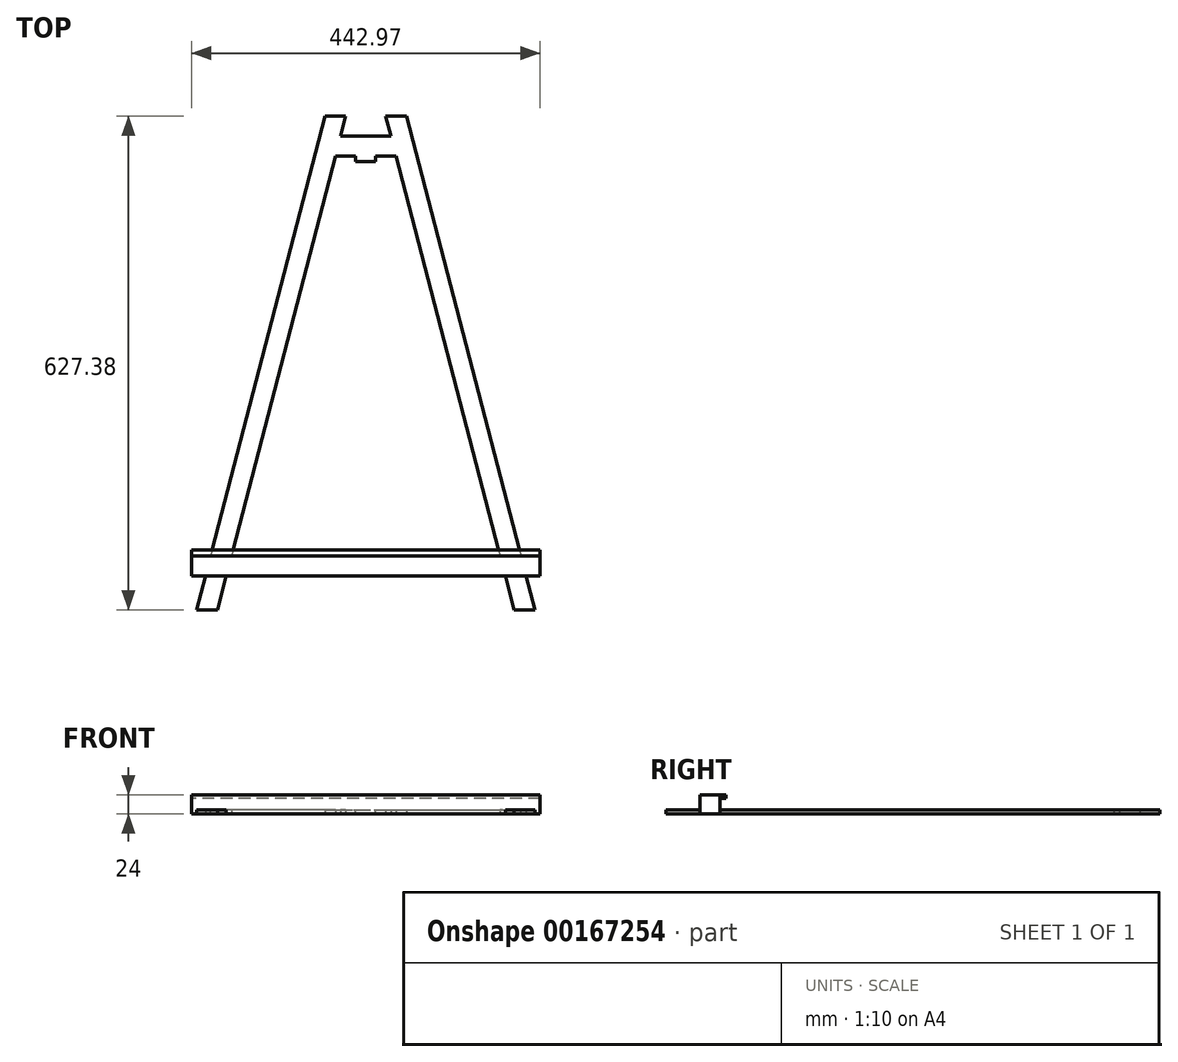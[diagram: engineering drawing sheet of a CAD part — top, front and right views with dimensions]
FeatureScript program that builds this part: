
annotation { "Feature Type Name" : "Feature", "Feature Type Description" : "" }
export const myFeature = defineFeature(function(context is Context, id is Id, definition is map)
    precondition{}
    {
        {
            var Q0;
            Q0=qCreatedBy(makeId("Top.planeOp"),FACE);
            var sketch = newSketch(context, id + "F0", { "sketchPlane" : qUnion([Q0])});
            skLineSegment(sketch, "E0.bottom", {"start": v(-187.71, 547.8) * mm, "end": v(193.29, 547.8) * mm});
            skLineSegment(sketch, "E0.top", {"start": v(-187.71, -87.2) * mm, "end": v(193.29, -87.2) * mm});
            skLineSegment(sketch, "E0.left", {"start": v(-187.71, 547.8) * mm, "end": v(-187.71, -87.2) * mm});
            skLineSegment(sketch, "E0.right", {"start": v(193.29, 547.8) * mm, "end": v(193.29, -87.2) * mm});
            skLineSegment(sketch, "E1", {"start": v(2.79, 547.8) * mm, "end": v(-22.61, 547.8) * mm});
            skLineSegment(sketch, "E2", {"start": v(2.79, 547.8) * mm, "end": v(28.19, 547.8) * mm});
            skLineSegment(sketch, "E3", {"start": v(-22.61, 547.8) * mm, "end": v(-187.71, -87.2) * mm});
            skLineSegment(sketch, "E4", {"start": v(28.19, 547.8) * mm, "end": v(193.29, -87.2) * mm});
            skLineSegment(sketch, "E5", {"start": v(-167.9, -11) * mm, "end": v(173.47, -11) * mm});
            skLineSegment(sketch, "E6.0", {"start": v(-47.2, 554.2) * mm, "end": v(-212.3, -80.8) * mm});
            skLineSegment(sketch, "E7.0", {"start": v(52.77, 554.2) * mm, "end": v(217.87, -80.8) * mm});
            skLineSegment(sketch, "E8.0", {"start": v(-174.5, -36.4) * mm, "end": v(180.08, -36.4) * mm});
            skLineSegment(sketch, "E9", {"start": v(-47.2, 554.2) * mm, "end": v(-22.61, 547.8) * mm});
            skLineSegment(sketch, "E10", {"start": v(28.19, 547.8) * mm, "end": v(52.77, 554.2) * mm});
            skLineSegment(sketch, "E11", {"start": v(-212.3, -80.8) * mm, "end": v(-187.71, -87.2) * mm});
            skLineSegment(sketch, "E12", {"start": v(193.29, -87.2) * mm, "end": v(217.87, -80.8) * mm});
            skLineSegment(sketch, "E13", {"start": v(-29.22, 522.4) * mm, "end": v(34.8, 522.4) * mm});
            skLineSegment(sketch, "E14.0", {"start": v(-35.82, 497) * mm, "end": v(41.4, 497) * mm});
            skLineSegment(sketch, "E15", {"start": v(2.79, 547.8) * mm, "end": v(2.79, 522.4) * mm, "construction": true});
            skLineSegment(sketch, "E16", {"start": v(2.79, -36.4) * mm, "end": v(2.79, -87.2) * mm, "construction": true});
            skSolve(sketch);
        }
        {
            var Q0;
            {var subQ0=sQuery(id+"F0.wireOp",EDGE,"E3");var subQ1=makeQuery(id+"F0.imprint","INTERSECT",VERTEX,{"derivedFrom":[subQ0,sQuery(id+"F0.wireOp",EDGE,"E13")]});Q0=makeQuery(id+"F0.imprint","IMPRINT",FACE,{"disambiguationData":[TD([[makeQuery(id+"F0.imprint","IMPRINT",EDGE,{"disambiguationData":[TD([[subQ1,-1.0]])],"derivedFrom":subQ0}),-1.0]])]});}
            var Q1;
            {var subQ0=sQuery(id+"F0.wireOp",EDGE,"E13");Q1=makeQuery(id+"F0.imprint","IMPRINT",FACE,{"disambiguationData":[TD([[makeQuery(id+"F0.imprint","IMPRINT",EDGE,{"derivedFrom":subQ0}),-1.0]])]});}
            var Q2;
            {var subQ0=sQuery(id+"F0.wireOp",EDGE,"E4");var subQ5=makeQuery(id+"F0.imprint","INTERSECT",VERTEX,{"derivedFrom":[subQ0,sQuery(id+"F0.wireOp",EDGE,"E13")]});Q2=makeQuery(id+"F0.imprint","IMPRINT",FACE,{"disambiguationData":[TD([[makeQuery(id+"F0.imprint","IMPRINT",EDGE,{"disambiguationData":[TD([[subQ5,-1.0]])],"derivedFrom":subQ0}),1.0]])]});}
            var Q3;
            {var subQ0=sQuery(id+"F0.wireOp",EDGE,"E5");Q3=makeQuery(id+"F0.imprint","IMPRINT",FACE,{"disambiguationData":[TD([[makeQuery(id+"F0.imprint","IMPRINT",EDGE,{"derivedFrom":subQ0}),-1.0]])]});}
            var Q4;
            {var subQ0=sQuery(id+"F0.wireOp",EDGE,"E11");Q4=makeQuery(id+"F0.imprint","IMPRINT",FACE,{"disambiguationData":[TD([[makeQuery(id+"F0.imprint","IMPRINT",EDGE,{"derivedFrom":subQ0}),1.0]])]});}
            var Q5;
            {var subQ0=sQuery(id+"F0.wireOp",EDGE,"E12");Q5=makeQuery(id+"F0.imprint","IMPRINT",FACE,{"disambiguationData":[TD([[makeQuery(id+"F0.imprint","IMPRINT",EDGE,{"derivedFrom":subQ0}),1.0]])]});}
            extrude(context, id + "F1", {"entities" : qUnion([Q0, Q1, Q2, Q3, Q4, Q5]), "depth" : 5 * mm});
        }
        {
            var Q0;
            Q0=makeQuery(id+"F1.opExtrude","CAP_FACE",FACE,{"disambiguationData":[OSD([sQuery(id+"F0.wireOp",EDGE,"E0.bottom"),sQuery(id+"F0.wireOp",EDGE,"E3"),sQuery(id+"F0.wireOp",EDGE,"E4"),sQuery(id+"F0.wireOp",EDGE,"E5"),sQuery(id+"F0.wireOp",EDGE,"E6.0"),sQuery(id+"F0.wireOp",EDGE,"E7.0"),sQuery(id+"F0.wireOp",EDGE,"E8.0"),sQuery(id+"F0.wireOp",EDGE,"E11"),sQuery(id+"F0.wireOp",EDGE,"E12"),sQuery(id+"F0.wireOp",EDGE,"E13"),sQuery(id+"F0.wireOp",EDGE,"E14.0")])],"isStart":true});
            var sketch = newSketch(context, id + "F2", { "sketchPlane" : qUnion([Q0])});
            skLineSegment(sketch, "E17.0", {"start": v(-167.9, 11) * mm, "end": v(173.47, 11) * mm});
            skLineSegment(sketch, "E18.0", {"start": v(-174.5, 36.4) * mm, "end": v(180.08, 36.4) * mm});
            skLineSegment(sketch, "E19", {"start": v(2.79, 3.1) * mm, "end": v(2.79, -57.6) * mm, "construction": true});
            skLineSegment(sketch, "E20", {"start": v(-174.5, 36.4) * mm, "end": v(-218.7, 36.4) * mm});
            skLineSegment(sketch, "E21", {"start": v(-218.7, 11) * mm, "end": v(-218.7, 36.4) * mm});
            skLineSegment(sketch, "E22", {"start": v(-218.7, 11) * mm, "end": v(-167.9, 11) * mm});
            skLineSegment(sketch, "E23.MirrorCS", {"start": v(180.08, 36.4) * mm, "end": v(224.27, 36.4) * mm});
            skLineSegment(sketch, "E24.MirrorCS", {"start": v(224.27, 11) * mm, "end": v(224.27, 36.4) * mm});
            skLineSegment(sketch, "E25.MirrorCS", {"start": v(224.27, 11) * mm, "end": v(173.47, 11) * mm});
            skSolve(sketch);
        }
        {
            var Q0;
            Q0=qSketchRegion(id+"F2",true);
            extrude(context, id + "F3", {"entities" : qUnion([Q0]), "operationType" : NewBodyOperationType.ADD, "oppositeDirection" : true, "depth" : 24 * mm});
        }
        {
            var Q0;
            Q0=makeQuery(id+"F1.opExtrude","SWEPT_FACE",FACE,{"disambiguationData":[OSD([sQuery(id+"F0.wireOp",EDGE,"E14.0")])]});
            var sketch = newSketch(context, id + "F4", { "sketchPlane" : qUnion([Q0])});
            skLineSegment(sketch, "E26.bottom", {"start": v(15.49, 0) * mm, "end": v(-9.91, 0) * mm});
            skLineSegment(sketch, "E26.top", {"start": v(15.49, 5) * mm, "end": v(-9.91, 5) * mm});
            skLineSegment(sketch, "E26.left", {"start": v(15.49, 0) * mm, "end": v(15.49, 5) * mm});
            skLineSegment(sketch, "E26.right", {"start": v(-9.91, 0) * mm, "end": v(-9.91, 5) * mm});
            skLineSegment(sketch, "E27", {"start": v(2.79, 0) * mm, "end": v(2.79, 5) * mm, "construction": true});
            skSolve(sketch);
        }
        {
            var Q0;
            Q0=qSketchRegion(id+"F4",true);
            extrude(context, id + "F5", {"entities" : qUnion([Q0]), "operationType" : NewBodyOperationType.ADD, "depth" : 7 * mm});
        }
        {
            var Q0;
            Q0=makeQuery(id+"F1.opExtrude","CAP_VERTEX",VERTEX,{"disambiguationData":[OSD([sQuery(id+"F0.wireOp",EDGE,"E0.top"),sQuery(id+"F0.wireOp",EDGE,"E0.left"),sQuery(id+"F0.wireOp",EDGE,"E3"),sQuery(id+"F0.wireOp",EDGE,"E11")])],"isStart":false});
            var Q1;
            Q1=makeQuery(id+"F1.opExtrude","CAP_VERTEX",VERTEX,{"disambiguationData":[OSD([sQuery(id+"F0.wireOp",EDGE,"E0.top"),sQuery(id+"F0.wireOp",EDGE,"E0.right"),sQuery(id+"F0.wireOp",EDGE,"E4"),sQuery(id+"F0.wireOp",EDGE,"E12")])],"isStart":false});
            var Q2;
            Q2=makeQuery(id+"F1.opExtrude","CAP_VERTEX",VERTEX,{"disambiguationData":[OSD([sQuery(id+"F0.wireOp",EDGE,"E0.top"),sQuery(id+"F0.wireOp",EDGE,"E0.right"),sQuery(id+"F0.wireOp",EDGE,"E4"),sQuery(id+"F0.wireOp",EDGE,"E12")])],"isStart":true});
            cPlane(context, id + "F6", {"entities" : qUnion([Q0, Q1, Q2]), "cplaneType" : CPlaneType.THREE_POINT, "offset" : 150 * mm, "width" : 150 * mm, "height" : 150 * mm});
        }
        {
            var Q0;
            Q0=qCreatedBy(id+"F6.planeOp",FACE);
            var sketch = newSketch(context, id + "F7", { "sketchPlane" : qUnion([Q0])});
            skLineSegment(sketch, "E28.bottom", {"start": v(-249.5, 41.86) * mm, "end": v(258.5, 41.86) * mm});
            skLineSegment(sketch, "E28.top", {"start": v(-249.5, -39.7) * mm, "end": v(258.5, -39.7) * mm});
            skLineSegment(sketch, "E28.left", {"start": v(-249.5, 41.86) * mm, "end": v(-249.5, -39.7) * mm});
            skLineSegment(sketch, "E28.right", {"start": v(258.5, 41.86) * mm, "end": v(258.5, -39.7) * mm});
            skSolve(sketch);
        }
        {
            var Q0;
            Q0=qSketchRegion(id+"F7",true);
            extrude(context, id + "F8", {"entities" : qUnion([Q0]), "operationType" : NewBodyOperationType.REMOVE, "oppositeDirection" : true, "depth" : 7.62 * mm});
        }
        {
            var Q0;
            Q0=makeQuery(id+"F3.boolean.opBoolean","MERGE",FACE,{"derivedFrom":[makeQuery(id+"F1.opExtrude","SWEPT_FACE",FACE,{"disambiguationData":[OSD([sQuery(id+"F0.wireOp",EDGE,"E5")])]}),makeQuery(id+"F3.opExtrude","SWEPT_FACE",FACE,{"disambiguationData":[OSD([sQuery(id+"F2.wireOp",EDGE,"E17.0"),sQuery(id+"F2.wireOp",EDGE,"E22"),sQuery(id+"F2.wireOp",EDGE,"E25.MirrorCS")])]})]});
            var sketch = newSketch(context, id + "F9", { "sketchPlane" : qUnion([Q0])});
            skLineSegment(sketch, "E29.bottom", {"start": v(-224.27, 24) * mm, "end": v(218.7, 24) * mm});
            skLineSegment(sketch, "E29.top", {"start": v(-224.27, 19.62) * mm, "end": v(218.7, 19.62) * mm});
            skLineSegment(sketch, "E29.left", {"start": v(-224.27, 24) * mm, "end": v(-224.27, 19.62) * mm});
            skLineSegment(sketch, "E29.right", {"start": v(218.7, 24) * mm, "end": v(218.7, 19.62) * mm});
            skSolve(sketch);
        }
        {
            var Q0;
            Q0=qSketchRegion(id+"F9",true);
            extrude(context, id + "F10", {"entities" : qUnion([Q0]), "depth" : 7.62 * mm});
        }
    });
